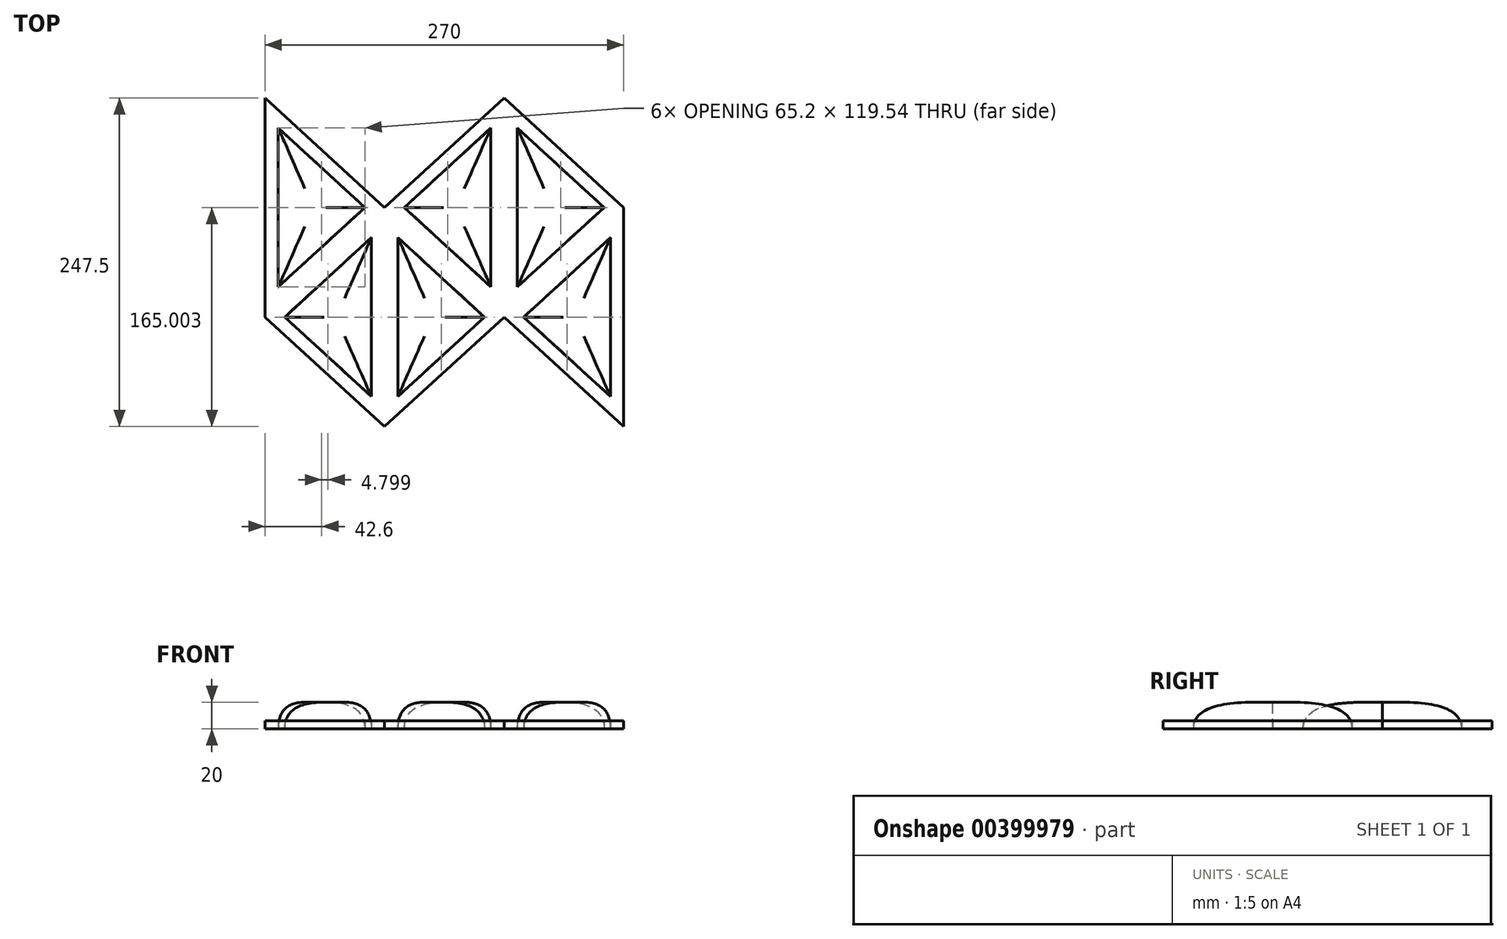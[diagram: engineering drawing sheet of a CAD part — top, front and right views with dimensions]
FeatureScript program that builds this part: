
annotation { "Feature Type Name" : "Feature", "Feature Type Description" : "" }
export const myFeature = defineFeature(function(context is Context, id is Id, definition is map)
    precondition{}
    {
        {
            var Q0;
            Q0=qCreatedBy(makeId("Top.planeOp"),FACE);
            var sketch = newSketch(context, id + "F0", { "sketchPlane" : qUnion([Q0])});
            skLineSegment(sketch, "E0", {"start": v(-96.44, 57.9) * mm, "end": v(-96.44, -310.18) * mm, "construction": true});
            skLineSegment(sketch, "E1.1.0.0", {"start": v(-6.44, 57.9) * mm, "end": v(-6.44, -310.18) * mm, "construction": true});
            skLineSegment(sketch, "E1.2.0.0", {"start": v(83.56, 57.9) * mm, "end": v(83.56, -310.18) * mm, "construction": true});
            skLineSegment(sketch, "E1.3.0.0", {"start": v(173.56, 57.9) * mm, "end": v(173.56, -310.18) * mm, "construction": true});
            skLineSegment(sketch, "E1.direction1", {"start": v(-96.44, -310.18) * mm, "end": v(-6.44, -310.18) * mm, "construction": true});
            skLineSegment(sketch, "E2", {"start": v(-121.38, 33.52) * mm, "end": v(197.88, 33.52) * mm, "construction": true});
            skLineSegment(sketch, "E3.0.1.0", {"start": v(-121.38, -48.98) * mm, "end": v(197.88, -48.98) * mm, "construction": true});
            skLineSegment(sketch, "E3.0.2.0", {"start": v(-121.38, -131.48) * mm, "end": v(197.88, -131.48) * mm, "construction": true});
            skLineSegment(sketch, "E3.0.3.0", {"start": v(-121.38, -213.98) * mm, "end": v(197.88, -213.98) * mm, "construction": true});
            skLineSegment(sketch, "E3.direction1", {"start": v(-121.38, 33.52) * mm, "end": v(-96.38, 33.52) * mm, "construction": true});
            skLineSegment(sketch, "E3.direction2", {"start": v(-121.38, 33.52) * mm, "end": v(-121.38, -48.98) * mm, "construction": true});
            skSolve(sketch);
        }
        {
            var Q0;
            Q0=qCreatedBy(makeId("Top.planeOp"),FACE);
            var sketch = newSketch(context, id + "F1", { "sketchPlane" : qUnion([Q0])});
            skLineSegment(sketch, "E4", {"start": v(-96.44, 33.52) * mm, "end": v(-6.44, -48.98) * mm});
            skLineSegment(sketch, "E5", {"start": v(-6.44, -48.98) * mm, "end": v(-96.44, -131.48) * mm});
            skLineSegment(sketch, "E6", {"start": v(-96.44, -131.48) * mm, "end": v(-96.44, 33.52) * mm});
            skLineSegment(sketch, "E7", {"start": v(-6.44, -48.98) * mm, "end": v(-6.44, -213.98) * mm});
            skLineSegment(sketch, "E8", {"start": v(-6.44, -213.98) * mm, "end": v(-96.44, -131.48) * mm});
            skLineSegment(sketch, "E9", {"start": v(-6.44, -48.98) * mm, "end": v(83.56, 33.52) * mm});
            skLineSegment(sketch, "E10", {"start": v(83.56, 33.52) * mm, "end": v(83.56, -131.48) * mm});
            skLineSegment(sketch, "E11", {"start": v(83.56, -131.48) * mm, "end": v(-6.44, -48.98) * mm});
            skLineSegment(sketch, "E12", {"start": v(83.56, -131.48) * mm, "end": v(-6.44, -213.98) * mm});
            skLineSegment(sketch, "E13", {"start": v(83.56, 33.52) * mm, "end": v(173.56, -48.98) * mm});
            skLineSegment(sketch, "E14", {"start": v(173.56, -48.98) * mm, "end": v(83.56, -131.48) * mm});
            skLineSegment(sketch, "E15", {"start": v(83.56, -131.48) * mm, "end": v(173.56, -213.98) * mm});
            skLineSegment(sketch, "E16", {"start": v(173.56, -213.98) * mm, "end": v(173.56, -48.98) * mm});
            skLineSegment(sketch, "E17.0", {"start": v(-21.24, -48.98) * mm, "end": v(-86.44, -108.74) * mm});
            skLineSegment(sketch, "E17.1", {"start": v(-86.44, 10.8) * mm, "end": v(-21.24, -48.98) * mm});
            skLineSegment(sketch, "E17.2", {"start": v(-86.44, -108.74) * mm, "end": v(-86.44, 10.8) * mm});
            skLineSegment(sketch, "E18.0", {"start": v(-16.44, -71.7) * mm, "end": v(-16.44, -191.24) * mm});
            skLineSegment(sketch, "E18.1", {"start": v(-16.44, -71.7) * mm, "end": v(-81.64, -131.48) * mm});
            skLineSegment(sketch, "E18.2", {"start": v(-16.44, -191.24) * mm, "end": v(-81.64, -131.48) * mm});
            skLineSegment(sketch, "E19.0", {"start": v(68.76, -131.48) * mm, "end": v(3.56, -71.7) * mm});
            skLineSegment(sketch, "E19.1", {"start": v(68.76, -131.48) * mm, "end": v(3.56, -191.24) * mm});
            skLineSegment(sketch, "E19.2", {"start": v(3.56, -71.7) * mm, "end": v(3.56, -191.24) * mm});
            skLineSegment(sketch, "E20.0", {"start": v(73.56, 10.8) * mm, "end": v(73.56, -108.74) * mm});
            skLineSegment(sketch, "E20.1", {"start": v(8.36, -48.98) * mm, "end": v(73.56, 10.8) * mm});
            skLineSegment(sketch, "E20.2", {"start": v(73.56, -108.74) * mm, "end": v(8.36, -48.98) * mm});
            skLineSegment(sketch, "E21.0", {"start": v(93.56, 10.8) * mm, "end": v(93.56, -108.74) * mm});
            skLineSegment(sketch, "E21.1", {"start": v(93.56, 10.8) * mm, "end": v(158.76, -48.98) * mm});
            skLineSegment(sketch, "E21.2", {"start": v(158.76, -48.98) * mm, "end": v(93.56, -108.74) * mm});
            skLineSegment(sketch, "E22.0", {"start": v(163.56, -191.24) * mm, "end": v(163.56, -71.7) * mm});
            skLineSegment(sketch, "E22.1", {"start": v(98.36, -131.48) * mm, "end": v(163.56, -191.24) * mm});
            skLineSegment(sketch, "E22.2", {"start": v(163.56, -71.7) * mm, "end": v(98.36, -131.48) * mm});
            skSolve(sketch);
        }
        {
            var Q0;
            Q0=makeQuery(id+"F1.imprint","IMPRINT",FACE,{"disambiguationData":[TD([[makeQuery(id+"F1.imprint","IMPRINT",EDGE,{"derivedFrom":sQuery(id+"F1.wireOp",EDGE,"E17.0")}),-1.0]])]});
            var Q1;
            Q1=makeQuery(id+"F1.imprint","IMPRINT",FACE,{"disambiguationData":[TD([[makeQuery(id+"F1.imprint","IMPRINT",EDGE,{"derivedFrom":sQuery(id+"F1.wireOp",EDGE,"E18.0")}),-1.0]])]});
            var Q2;
            Q2=makeQuery(id+"F1.imprint","IMPRINT",FACE,{"disambiguationData":[TD([[makeQuery(id+"F1.imprint","IMPRINT",EDGE,{"derivedFrom":sQuery(id+"F1.wireOp",EDGE,"E19.0")}),1.0]])]});
            var Q3;
            Q3=makeQuery(id+"F1.imprint","IMPRINT",FACE,{"disambiguationData":[TD([[makeQuery(id+"F1.imprint","IMPRINT",EDGE,{"derivedFrom":sQuery(id+"F1.wireOp",EDGE,"E20.0")}),-1.0]])]});
            var Q4;
            Q4=makeQuery(id+"F1.imprint","IMPRINT",FACE,{"disambiguationData":[TD([[makeQuery(id+"F1.imprint","IMPRINT",EDGE,{"derivedFrom":sQuery(id+"F1.wireOp",EDGE,"E21.0")}),1.0]])]});
            var Q5;
            Q5=makeQuery(id+"F1.imprint","IMPRINT",FACE,{"disambiguationData":[TD([[makeQuery(id+"F1.imprint","IMPRINT",EDGE,{"derivedFrom":sQuery(id+"F1.wireOp",EDGE,"E22.0")}),1.0]])]});
            extrude(context, id + "F2", {"entities" : qUnion([Q0, Q1, Q2, Q3, Q4, Q5]), "depth" : 20 * mm});
        }
        {
            var Q0;
            Q0=makeQuery(id+"F1.imprint","IMPRINT",FACE,{"disambiguationData":[TD([[makeQuery(id+"F1.imprint","IMPRINT",EDGE,{"derivedFrom":sQuery(id+"F1.wireOp",EDGE,"E4")}),-1.0]])]});
            var Q1;
            Q1=makeQuery(id+"F1.imprint","IMPRINT",FACE,{"disambiguationData":[TD([[makeQuery(id+"F1.imprint","IMPRINT",EDGE,{"derivedFrom":sQuery(id+"F1.wireOp",EDGE,"E5")}),1.0]])]});
            var Q2;
            Q2=makeQuery(id+"F1.imprint","IMPRINT",FACE,{"disambiguationData":[TD([[makeQuery(id+"F1.imprint","IMPRINT",EDGE,{"derivedFrom":sQuery(id+"F1.wireOp",EDGE,"E7")}),1.0]])]});
            var Q3;
            Q3=makeQuery(id+"F1.imprint","IMPRINT",FACE,{"disambiguationData":[TD([[makeQuery(id+"F1.imprint","IMPRINT",EDGE,{"derivedFrom":sQuery(id+"F1.wireOp",EDGE,"E10")}),1.0]])]});
            var Q4;
            Q4=makeQuery(id+"F1.imprint","IMPRINT",FACE,{"disambiguationData":[TD([[makeQuery(id+"F1.imprint","IMPRINT",EDGE,{"derivedFrom":sQuery(id+"F1.wireOp",EDGE,"E9")}),-1.0]])]});
            var Q5;
            Q5=makeQuery(id+"F1.imprint","IMPRINT",FACE,{"disambiguationData":[TD([[makeQuery(id+"F1.imprint","IMPRINT",EDGE,{"derivedFrom":sQuery(id+"F1.wireOp",EDGE,"E14")}),1.0]])]});
            extrude(context, id + "F3", {"entities" : qUnion([Q0, Q1, Q2, Q3, Q4, Q5]), "depth" : 6 * mm});
        }
        {
            var Q0;
            Q0=makeQuery(id+"F2.opExtrude","CAP_FACE",FACE,{"disambiguationData":[OSD([sQuery(id+"F1.wireOp",EDGE,"E17.0"),sQuery(id+"F1.wireOp",EDGE,"E17.1"),sQuery(id+"F1.wireOp",EDGE,"E17.2")])],"isStart":false});
            var Q1;
            Q1=makeQuery(id+"F2.opExtrude","CAP_FACE",FACE,{"disambiguationData":[OSD([sQuery(id+"F1.wireOp",EDGE,"E18.0"),sQuery(id+"F1.wireOp",EDGE,"E18.1"),sQuery(id+"F1.wireOp",EDGE,"E18.2")])],"isStart":false});
            var Q2;
            Q2=makeQuery(id+"F2.opExtrude","CAP_FACE",FACE,{"disambiguationData":[OSD([sQuery(id+"F1.wireOp",EDGE,"E19.0"),sQuery(id+"F1.wireOp",EDGE,"E19.1"),sQuery(id+"F1.wireOp",EDGE,"E19.2")])],"isStart":false});
            var Q3;
            Q3=makeQuery(id+"F2.opExtrude","CAP_FACE",FACE,{"disambiguationData":[OSD([sQuery(id+"F1.wireOp",EDGE,"E20.0"),sQuery(id+"F1.wireOp",EDGE,"E20.1"),sQuery(id+"F1.wireOp",EDGE,"E20.2")])],"isStart":false});
            var Q4;
            Q4=makeQuery(id+"F2.opExtrude","CAP_FACE",FACE,{"disambiguationData":[OSD([sQuery(id+"F1.wireOp",EDGE,"E21.0"),sQuery(id+"F1.wireOp",EDGE,"E21.1"),sQuery(id+"F1.wireOp",EDGE,"E21.2")])],"isStart":false});
            var Q5;
            Q5=makeQuery(id+"F2.opExtrude","CAP_FACE",FACE,{"disambiguationData":[OSD([sQuery(id+"F1.wireOp",EDGE,"E22.0"),sQuery(id+"F1.wireOp",EDGE,"E22.1"),sQuery(id+"F1.wireOp",EDGE,"E22.2")])],"isStart":false});
            fillet(context, id + "F4", {"entities" : qUnion([Q0, Q1, Q2, Q3, Q4, Q5]), "radius" : 20 * mm, "tangentPropagation" : true, "rho" : 0.5, "crossSection" : FilletCrossSection.CONIC, "allowEdgeOverflow" : false});
        }
    });
